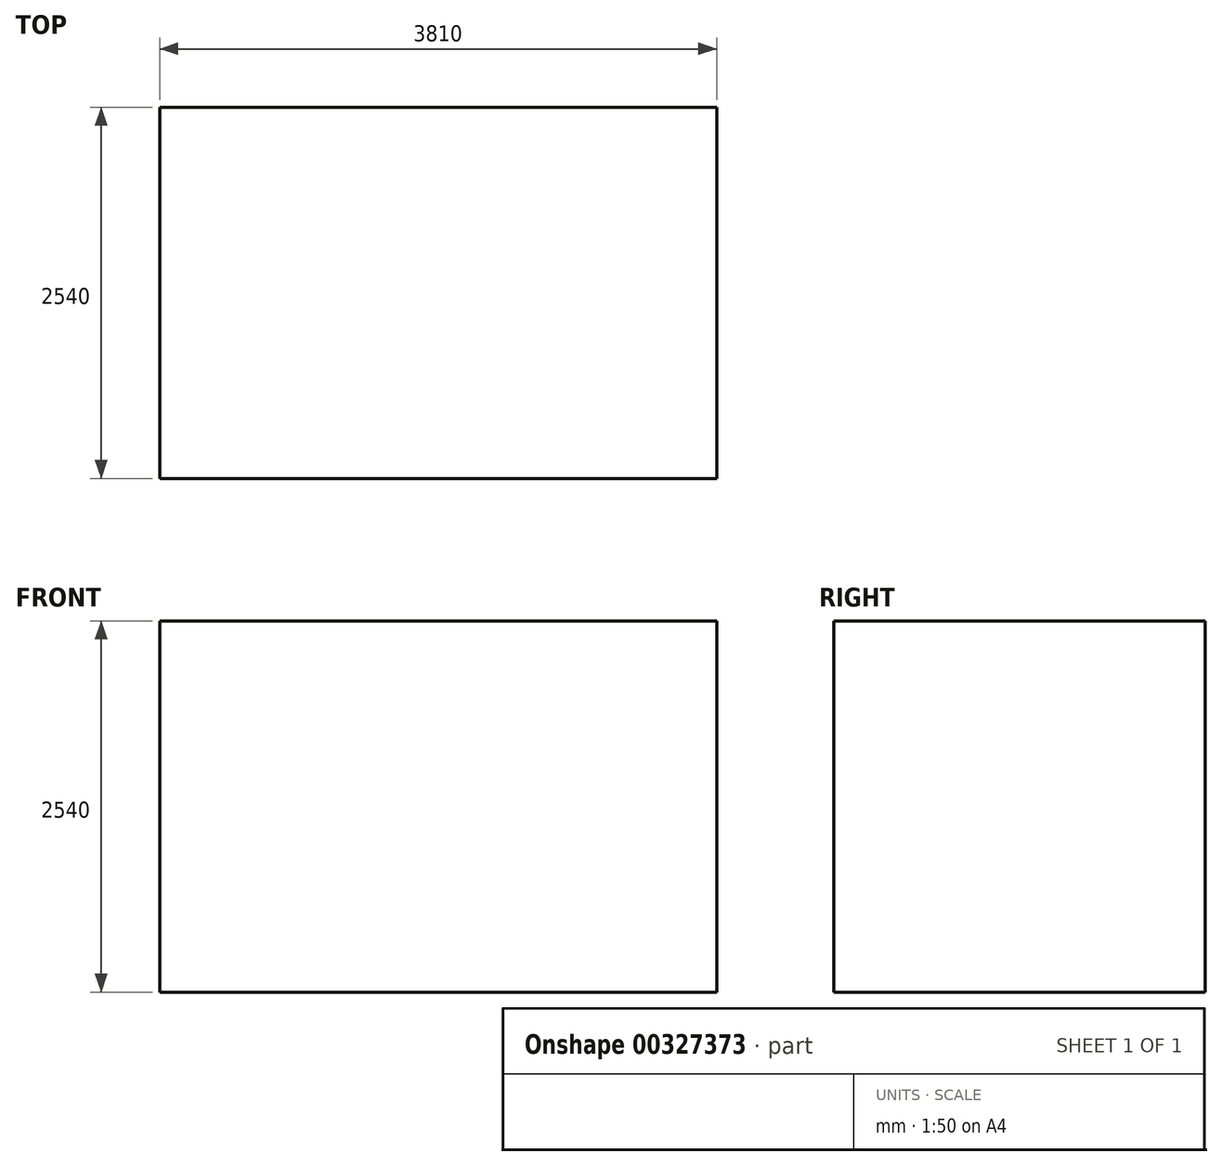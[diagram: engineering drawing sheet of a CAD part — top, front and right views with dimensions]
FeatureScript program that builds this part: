
annotation { "Feature Type Name" : "Feature", "Feature Type Description" : "" }
export const myFeature = defineFeature(function(context is Context, id is Id, definition is map)
    precondition{}
    {
        {
            var Q0;
            Q0=qCreatedBy(makeId("Top.planeOp"),FACE);
            var sketch = newSketch(context, id + "F0", { "sketchPlane" : qUnion([Q0])});
            skLineSegment(sketch, "E0.bottom", {"start": v(0, 0) * mm, "end": v(-3810, 0) * mm});
            skLineSegment(sketch, "E0.top", {"start": v(0, 2540) * mm, "end": v(-3810, 2540) * mm});
            skLineSegment(sketch, "E0.left", {"start": v(0, 0) * mm, "end": v(0, 2540) * mm});
            skLineSegment(sketch, "E0.right", {"start": v(-3810, 0) * mm, "end": v(-3810, 2540) * mm});
            skSolve(sketch);
        }
        {
            var Q0;
            Q0=makeQuery(id+"F0.imprint","IMPRINT",FACE,{"disambiguationData":[TD([[makeQuery(id+"F0.imprint","IMPRINT",EDGE,{"derivedFrom":sQuery(id+"F0.wireOp",EDGE,"E0.bottom")}),-1.0]])]});
            extrude(context, id + "F1", {"entities" : qUnion([Q0]), "depth" : 2540 * mm});
        }
        {
            var Q0;
            Q0=makeQuery(id+"F1.opExtrude","SWEPT_FACE",FACE,{"disambiguationData":[OSD([sQuery(id+"F0.wireOp",EDGE,"E0.right")])]});
            shell(context, id + "F2", {"entities" : qUnion([Q0]), "thickness" : 2.54 * mm});
        }
    });
